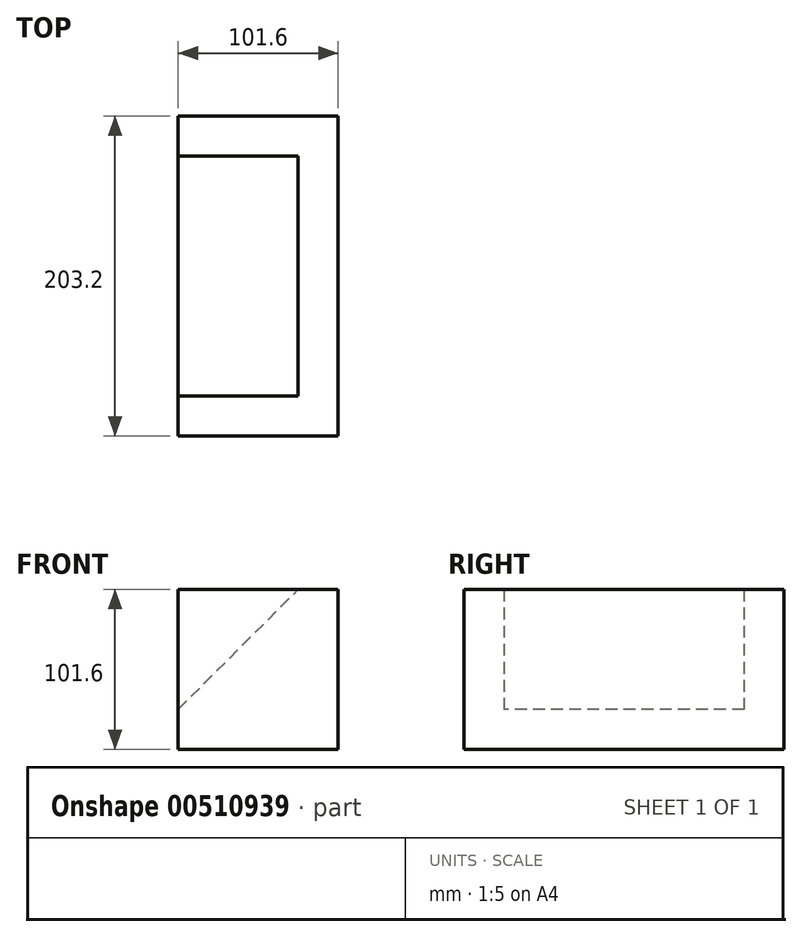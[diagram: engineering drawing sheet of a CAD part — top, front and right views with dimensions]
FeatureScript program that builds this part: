
annotation { "Feature Type Name" : "Feature", "Feature Type Description" : "" }
export const myFeature = defineFeature(function(context is Context, id is Id, definition is map)
    precondition{}
    {
        {
            var Q0;
            Q0=qCreatedBy(makeId("Front.planeOp"),FACE);
            var sketch = newSketch(context, id + "F0", { "sketchPlane" : qUnion([Q0])});
            skLineSegment(sketch, "E0.bottom", {"start": v(0, 0) * mm, "end": v(-101.6, 0) * mm});
            skLineSegment(sketch, "E0.top", {"start": v(0, -101.6) * mm, "end": v(-101.6, -101.6) * mm});
            skLineSegment(sketch, "E0.left", {"start": v(0, 0) * mm, "end": v(0, -101.6) * mm});
            skLineSegment(sketch, "E0.right", {"start": v(-101.6, 0) * mm, "end": v(-101.6, -101.6) * mm});
            skSolve(sketch);
        }
        {
            var Q0;
            Q0 = qSketchRegion(id + "F0", true);
            extrude(context, id + "F1", {"entities" : qUnion([Q0]), "depth" : 203.2 * mm});
        }
        {
            var Q0;
            Q0=makeQuery(id+"F1.opExtrude","SWEPT_FACE",FACE,{"disambiguationData":[OSD([sQuery(id+"F0.wireOp",EDGE,"E0.right")])]});
            var sketch = newSketch(context, id + "F2", { "sketchPlane" : qUnion([Q0])});
            skLineSegment(sketch, "E1.bottom", {"start": v(25.4, 0) * mm, "end": v(177.8, 0) * mm});
            skLineSegment(sketch, "E1.top", {"start": v(25.4, -76.2) * mm, "end": v(177.8, -76.2) * mm});
            skLineSegment(sketch, "E1.left", {"start": v(25.4, 0) * mm, "end": v(25.4, -76.2) * mm});
            skLineSegment(sketch, "E1.right", {"start": v(177.8, 0) * mm, "end": v(177.8, -76.2) * mm});
            skSolve(sketch);
        }
        {
            var Q0;
            Q0 = qSketchRegion(id + "F2", true);
            extrude(context, id + "F3", {"entities" : qUnion([Q0]), "operationType" : NewBodyOperationType.REMOVE, "oppositeDirection" : true, "depth" : 76.2 * mm});
        }
        {
            var Q0;
            Q0=makeQuery(id+"F3.boolean.opBoolean","COPY",FACE,{"derivedFrom":makeQuery(id+"F3.opExtrude","SWEPT_FACE",FACE,{"disambiguationData":[OSD([sQuery(id+"F2.wireOp",EDGE,"E1.right")])]})});
            var sketch = newSketch(context, id + "F4", { "sketchPlane" : qUnion([Q0])});
            skLineSegment(sketch, "E2", {"start": v(101.6, -76.2) * mm, "end": v(25.4, 0) * mm});
            skSolve(sketch);
        }
        {
            var Q0;
            Q0=makeQuery(id+"F4.imprint","IMPRINT",FACE,{"disambiguationData":[TD([[makeQuery(id+"F4.imprint","IMPRINT",EDGE,{"derivedFrom":sQuery(id+"F4.wireOp",EDGE,"E2")}),1.0]])]});
            extrude(context, id + "F5", {"entities" : qUnion([Q0]), "operationType" : NewBodyOperationType.ADD, "depth" : 152.4 * mm});
        }
    });
